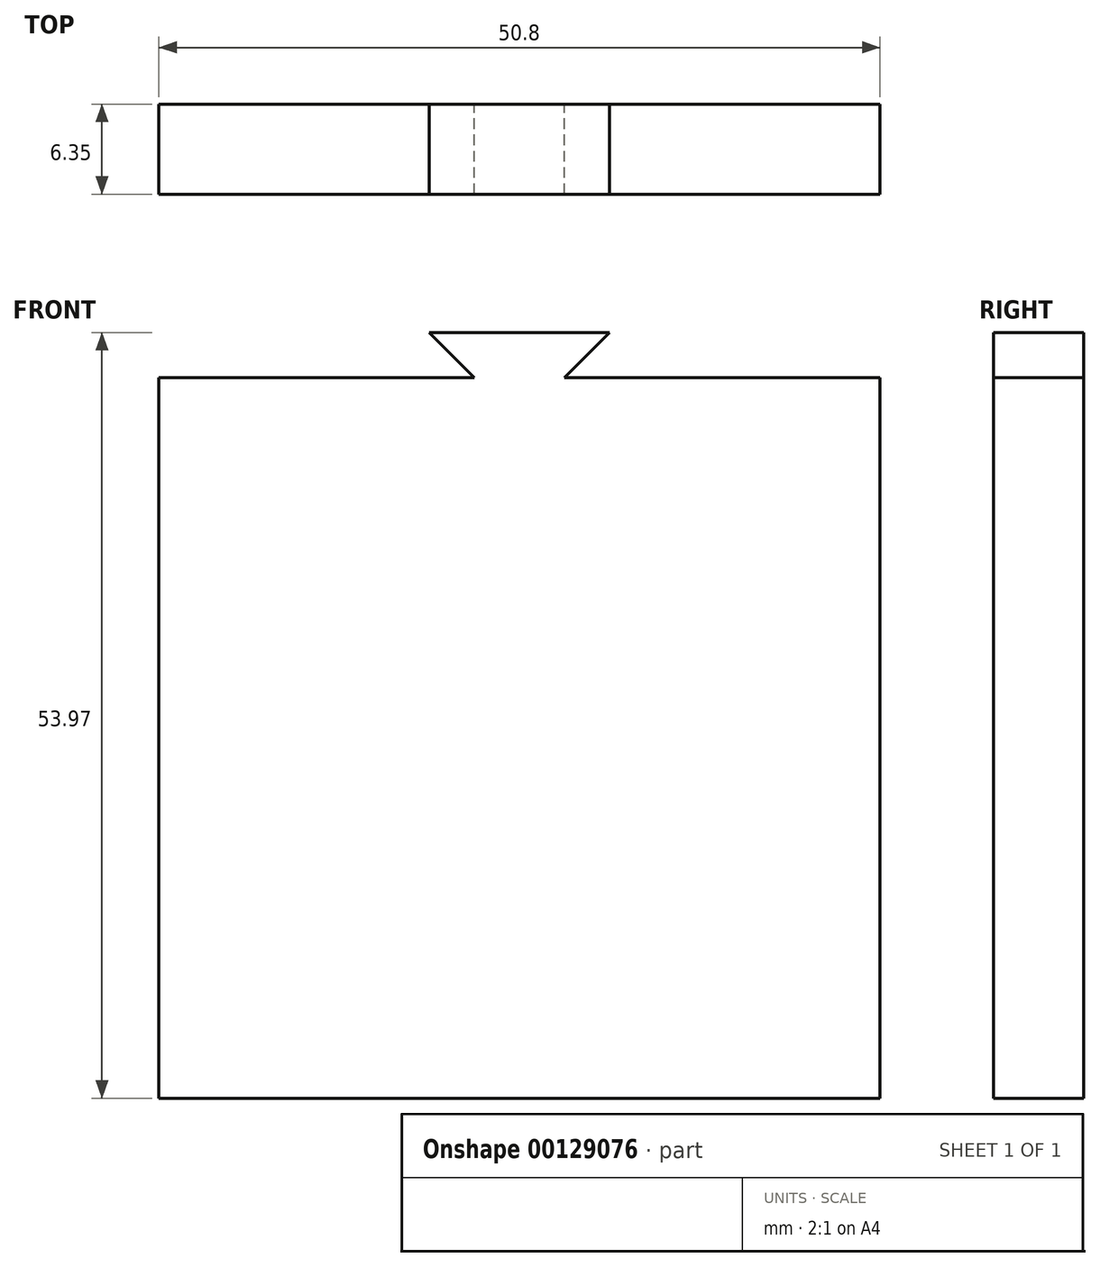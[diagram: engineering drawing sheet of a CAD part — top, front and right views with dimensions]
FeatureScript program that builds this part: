
annotation { "Feature Type Name" : "Feature", "Feature Type Description" : "" }
export const myFeature = defineFeature(function(context is Context, id is Id, definition is map)
    precondition{}
    {
        {
            var Q0;
            Q0=qCreatedBy(makeId("Front.planeOp"),FACE);
            var sketch = newSketch(context, id + "F0", { "sketchPlane" : qUnion([Q0])});
            skLineSegment(sketch, "E0.bottom", {"start": v(-25.4, 25.4) * mm, "end": v(-3.18, 25.4) * mm});
            skLineSegment(sketch, "E0.top", {"start": v(-25.4, -25.4) * mm, "end": v(25.4, -25.4) * mm});
            skLineSegment(sketch, "E0.left", {"start": v(-25.4, 25.4) * mm, "end": v(-25.4, -25.4) * mm});
            skLineSegment(sketch, "E0.right", {"start": v(25.4, 25.4) * mm, "end": v(25.4, -25.4) * mm});
            skPoint(sketch, "E0.middle", {"position": v(0, 0) * mm});
            skLineSegment(sketch, "E1", {"start": v(-3.18, 25.4) * mm, "end": v(-6.35, 28.58) * mm});
            skLineSegment(sketch, "E2", {"start": v(-6.35, 28.57) * mm, "end": v(6.35, 28.57) * mm});
            skLineSegment(sketch, "E3", {"start": v(6.35, 28.58) * mm, "end": v(3.18, 25.4) * mm});
            skLineSegment(sketch, "E4.trimOffspring", {"start": v(3.17, 25.4) * mm, "end": v(25.4, 25.4) * mm});
            skPoint(sketch, "E5", {"position": v(0, 28.57) * mm});
            skPoint(sketch, "E6", {"position": v(0, -25.4) * mm});
            skSolve(sketch);
        }
        {
            var Q0;
            Q0 = qSketchRegion(id + "F0", true);
            extrude(context, id + "F1", {"entities" : qUnion([Q0]), "depth" : 6.35 * mm});
        }
    });
